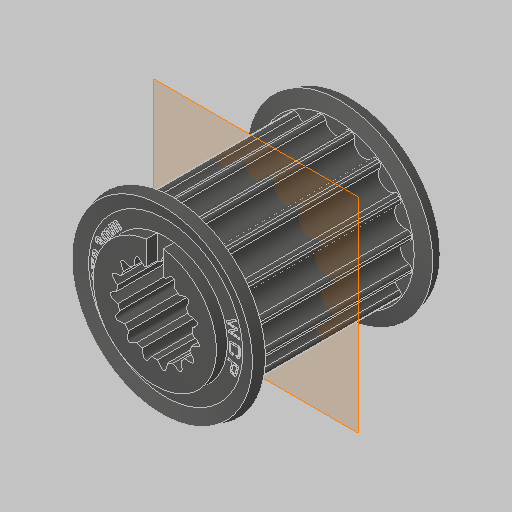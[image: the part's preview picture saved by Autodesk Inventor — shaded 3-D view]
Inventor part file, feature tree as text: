
AUTODESK INVENTOR PART (.ipt)
format: ipt  version: 2023.5 (Build 275446000, 446)  size: 593,408 bytes
history: native  units: in
note: dims shown in document units (in); Inventor stores cm internally (conversion verified against a paired STEP export)
features: other x2, mirror x1
ambient origin geometry x8: Origin, YZ Plane, XZ Plane, XY Plane, X Axis, Y Axis, Z Axis, Center Point
bodies: Solid1 (feature_tree), Solid2 (feature_tree), Solid3 (feature_tree)
feature tree (3):
  mirror  "Mirror3"
  other  "Cut-Extrude1"
  other  "Cut-Extrude2"
